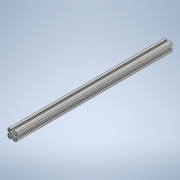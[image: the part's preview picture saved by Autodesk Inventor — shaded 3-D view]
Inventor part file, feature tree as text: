
AUTODESK INVENTOR PART (.ipt)
format: ipt  version: 2020 (Build 240168000, 168)  size: 222,720 bytes
history: native  units: mm
features: extrude x1, sketch x1
ambient origin geometry x8: Origin, YZ Plane, XZ Plane, XY Plane, X Axis, Y Axis, Z Axis, Center Point
bodies: Solid1 (feature_tree)
feature tree (2):
  extrude  "Extrusion1"  [1 undecoded]
  sketch  "Sketch1"  dims[d1=40.0mm d2=0.75mm d3=7.45mm d4=2.25mm d5=1.0mm d6=2.1mm d7=0.75mm d8=0.65mm d9=1.25mm d10=2.25mm d11=360.0deg d12=4.0mm d13=20.0mm d14=360.0mm d15=0.0mm]
note: 1 required parameter value undecoded (feature->parameter linkage not recoverable at this tier; creation-order binding heuristic only, values carry confidence <= 0.55)
